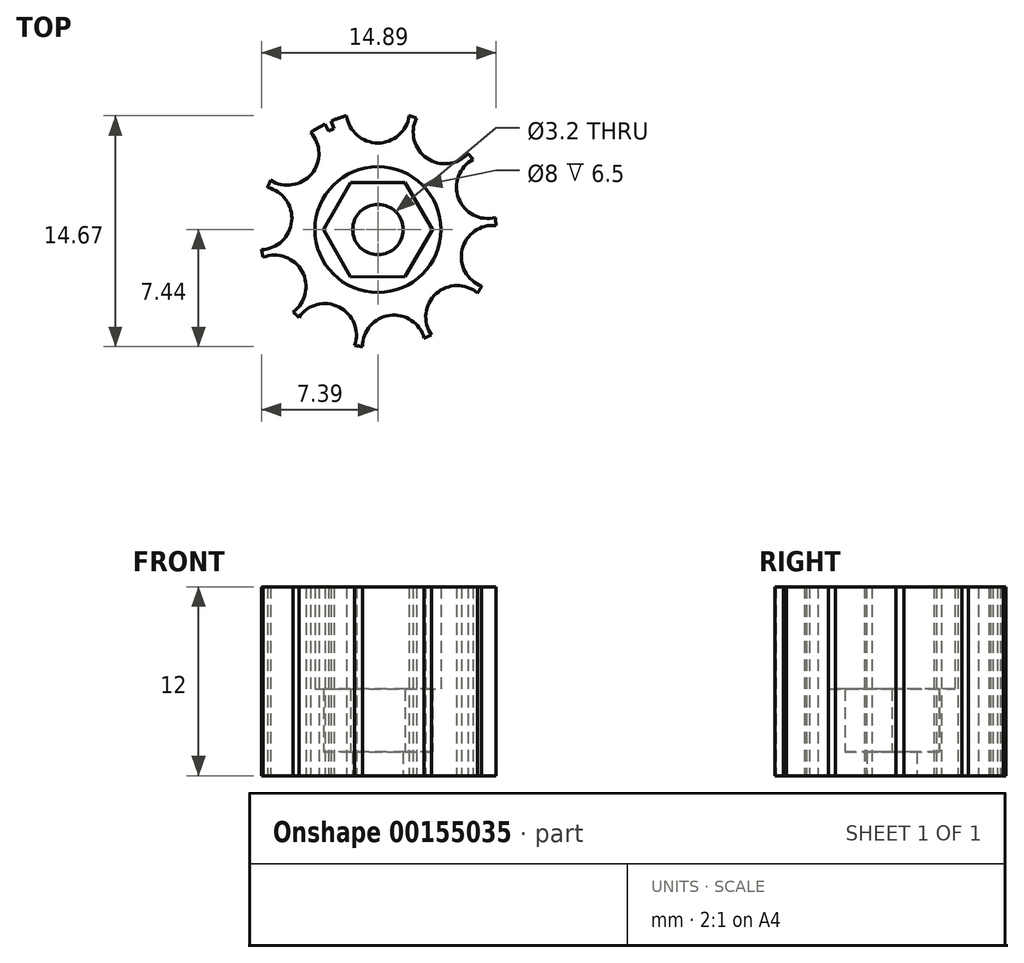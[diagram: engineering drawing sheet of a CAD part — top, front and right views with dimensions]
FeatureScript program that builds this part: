
annotation { "Feature Type Name" : "Feature", "Feature Type Description" : "" }
export const myFeature = defineFeature(function(context is Context, id is Id, definition is map)
    precondition{}
    {
        {
            var Q0;
            Q0=qCreatedBy(makeId("Top.planeOp"),FACE);
            var sketch = newSketch(context, id + "F0", { "sketchPlane" : qUnion([Q0])});
            skCircle(sketch, "E0", {"center": v(0, 0) * mm, "radius": 7.5 * mm});
            skCircle(sketch, "E1", {"center": v(0, 0) * mm, "radius": 1.6 * mm});
            skArc(sketch, "E2", {"start": v(-1.98, 7.23) * mm, "mid": v(0, 5.5) * mm, "end": v(1.98, 7.23) * mm});
            skArc(sketch, "E3.1.0", {"start": v(2.46, 7.09) * mm, "mid": v(3.11, 4.54) * mm, "end": v(5.73, 4.84) * mm});
            skArc(sketch, "E3.2.0", {"start": v(6.03, 4.45) * mm, "mid": v(5.13, 1.98) * mm, "end": v(7.46, 0.76) * mm});
            skArc(sketch, "E3.3.0", {"start": v(7.5, 0.26) * mm, "mid": v(5.35, -1.27) * mm, "end": v(6.58, -3.6) * mm});
            skArc(sketch, "E3.4.0", {"start": v(6.33, -4.02) * mm, "mid": v(3.7, -4.07) * mm, "end": v(3.4, -6.69) * mm});
            skArc(sketch, "E3.5.0", {"start": v(2.94, -6.9) * mm, "mid": v(0.74, -5.45) * mm, "end": v(-0.99, -7.44) * mm});
            skArc(sketch, "E3.6.0", {"start": v(-1.48, -7.35) * mm, "mid": v(-2.47, -4.91) * mm, "end": v(-5.02, -5.57) * mm});
            skArc(sketch, "E3.7.0", {"start": v(-5.38, -5.23) * mm, "mid": v(-4.82, -2.66) * mm, "end": v(-7.3, -1.76) * mm});
            skArc(sketch, "E3.8.0", {"start": v(-7.4, -1.27) * mm, "mid": v(-5.47, 0.53) * mm, "end": v(-7, 2.67) * mm});
            skArc(sketch, "E3.9.0", {"start": v(-6.82, 3.13) * mm, "mid": v(-4.21, 3.54) * mm, "end": v(-4.27, 6.17) * mm});
            skLineSegment(sketch, "E3.anchor1", {"start": v(0, 0) * mm, "end": v(-1.98, 7.23) * mm, "construction": true});
            skLineSegment(sketch, "E3.anchor2", {"start": v(0, 0) * mm, "end": v(-6.82, 3.13) * mm, "construction": true});
            skLineSegment(sketch, "E4", {"start": v(-3.35, 6.71) * mm, "end": v(-3.14, 6.26) * mm});
            skLineSegment(sketch, "E5.MirrorCS", {"start": v(-2.99, 6.88) * mm, "end": v(-2.78, 6.43) * mm});
            skLineSegment(sketch, "E6", {"start": v(-3.14, 6.26) * mm, "end": v(-2.78, 6.43) * mm});
            skLineSegment(sketch, "E7", {"start": v(-4.27, 6.17) * mm, "end": v(-1.98, 7.23) * mm, "construction": true});
            skLineSegment(sketch, "E8", {"start": v(-3.12, 6.7) * mm, "end": v(-2.79, 5.98) * mm, "construction": true});
            skSolve(sketch);
        }
        {
            var Q0;
            Q0=makeQuery(id+"F0.imprint","IMPRINT",FACE,{"disambiguationData":[TD([[makeQuery(id+"F0.imprint","IMPRINT",EDGE,{"derivedFrom":sQuery(id+"F0.wireOp",EDGE,"E1")}),-1.0]])]});
            extrude(context, id + "F1", {"entities" : qUnion([Q0]), "depth" : 12 * mm});
        }
        {
            var Q0;
            Q0=makeQuery(id+"F1.opExtrude","CAP_FACE",FACE,{"disambiguationData":[OSD([sQuery(id+"F0.wireOp",EDGE,"E0"),sQuery(id+"F0.wireOp",EDGE,"E1"),sQuery(id+"F0.wireOp",EDGE,"E2"),sQuery(id+"F0.wireOp",EDGE,"E3.1.0"),sQuery(id+"F0.wireOp",EDGE,"E3.2.0"),sQuery(id+"F0.wireOp",EDGE,"E3.3.0"),sQuery(id+"F0.wireOp",EDGE,"E3.4.0"),sQuery(id+"F0.wireOp",EDGE,"E3.5.0"),sQuery(id+"F0.wireOp",EDGE,"E3.6.0"),sQuery(id+"F0.wireOp",EDGE,"E3.7.0"),sQuery(id+"F0.wireOp",EDGE,"E3.8.0"),sQuery(id+"F0.wireOp",EDGE,"E3.9.0")])],"isStart":true});
            cPlane(context, id + "F2", {"entities" : qUnion([Q0]), "cplaneType" : CPlaneType.OFFSET, "offset" : 1.5 * mm, "oppositeDirection" : true, "width" : 150 * mm, "height" : 150 * mm});
        }
        {
            var Q0;
            Q0=qCreatedBy(id+"F2.planeOp",FACE);
            cPlane(context, id + "F3", {"entities" : qUnion([Q0]), "cplaneType" : CPlaneType.OFFSET, "offset" : 4 * mm, "oppositeDirection" : true, "width" : 150 * mm, "height" : 150 * mm});
        }
        {
            var Q0;
            Q0=qCreatedBy(id+"F2.planeOp",FACE);
            var sketch = newSketch(context, id + "F4", { "sketchPlane" : qUnion([Q0])});
            skCircle(sketch, "E9.cCircle", {"center": v(0, 0) * mm, "radius": 3 * mm, "construction": true});
            skLineSegment(sketch, "E9.0", {"start": v(1.74, 3) * mm, "end": v(3.46, 0) * mm});
            skLineSegment(sketch, "E9.1", {"start": v(3.46, 0) * mm, "end": v(1.73, -3) * mm});
            skLineSegment(sketch, "E9.2", {"start": v(1.73, -3) * mm, "end": v(-1.74, -3) * mm});
            skLineSegment(sketch, "E9.3", {"start": v(-1.74, -3) * mm, "end": v(-3.46, 0) * mm});
            skLineSegment(sketch, "E9.4", {"start": v(-3.46, 0) * mm, "end": v(-1.73, 3) * mm});
            skLineSegment(sketch, "E9.5", {"start": v(-1.73, 3) * mm, "end": v(1.74, 3) * mm});
            skPoint(sketch, "E9.0.midPoint", {"position": v(2.6, 1.5) * mm});
            skSolve(sketch);
        }
        {
            var Q0;
            Q0 = qSketchRegion(id + "F4", true);
            var Q1;
            Q1=makeQuery(id+"F1.opExtrude","CAP_FACE",FACE,{"disambiguationData":[OSD([sQuery(id+"F0.wireOp",EDGE,"E0"),sQuery(id+"F0.wireOp",EDGE,"E1"),sQuery(id+"F0.wireOp",EDGE,"E2"),sQuery(id+"F0.wireOp",EDGE,"E3.1.0"),sQuery(id+"F0.wireOp",EDGE,"E3.2.0"),sQuery(id+"F0.wireOp",EDGE,"E3.3.0"),sQuery(id+"F0.wireOp",EDGE,"E3.4.0"),sQuery(id+"F0.wireOp",EDGE,"E3.5.0"),sQuery(id+"F0.wireOp",EDGE,"E3.6.0"),sQuery(id+"F0.wireOp",EDGE,"E3.7.0"),sQuery(id+"F0.wireOp",EDGE,"E3.8.0"),sQuery(id+"F0.wireOp",EDGE,"E3.9.0")])],"isStart":false});
            extrude(context, id + "F5", {"entities" : qUnion([Q0]), "operationType" : NewBodyOperationType.REMOVE, "oppositeDirection" : true, "endBoundEntityFace" : qUnion([Q1]), "depth" : 4 * mm});
        }
        {
            var Q0;
            Q0=qCreatedBy(id+"F3.planeOp",FACE);
            var sketch = newSketch(context, id + "F6", { "sketchPlane" : qUnion([Q0])});
            skCircle(sketch, "E10", {"center": v(0, 0) * mm, "radius": 4 * mm});
            skSolve(sketch);
        }
        {
            var Q0;
            Q0 = qSketchRegion(id + "F6", true);
            var Q1;
            Q1=sQuery(id+"F6.wireOp",EDGE,"E10");
            extrude(context, id + "F7", {"entities" : qUnion([Q0]), "operationType" : NewBodyOperationType.REMOVE, "surfaceEntities" : qUnion([Q1]), "oppositeDirection" : true, "depth" : 25 * mm});
        }
    });
